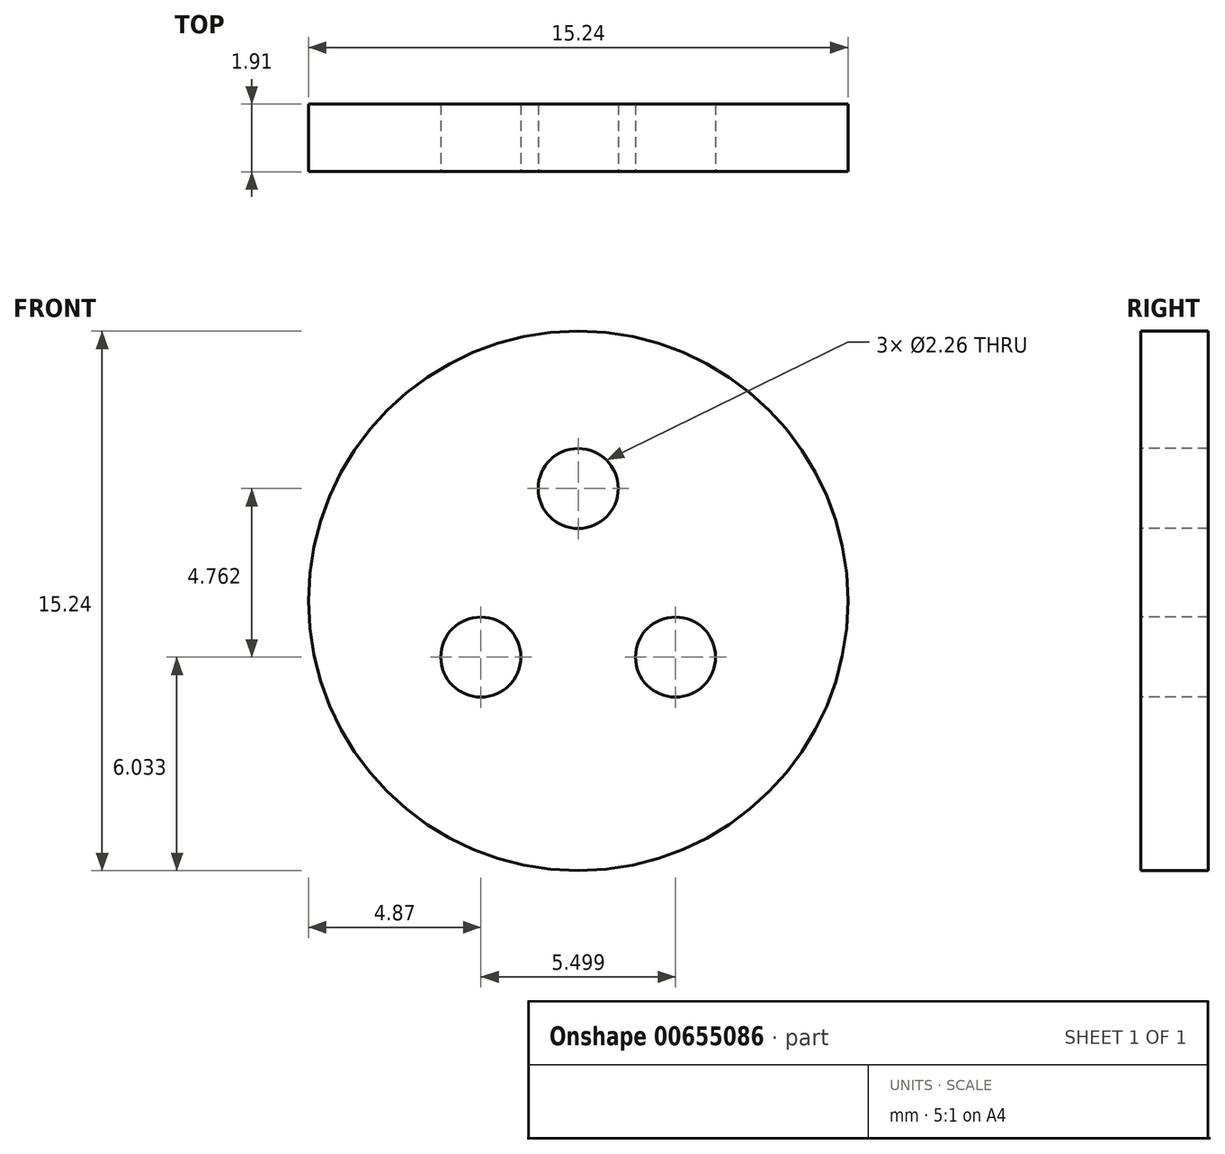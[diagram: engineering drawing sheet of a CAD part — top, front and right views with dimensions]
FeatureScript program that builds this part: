
annotation { "Feature Type Name" : "Feature", "Feature Type Description" : "" }
export const myFeature = defineFeature(function(context is Context, id is Id, definition is map)
    precondition{}
    {
        {
            var Q0;
            Q0=qCreatedBy(makeId("Front.planeOp"),FACE);
            var sketch = newSketch(context, id + "F0", { "sketchPlane" : qUnion([Q0])});
            skCircle(sketch, "E0", {"center": v(0, 0) * mm, "radius": 7.62 * mm});
            skSolve(sketch);
        }
        {
            var Q0;
            Q0 = qSketchRegion(id + "F0", true);
            extrude(context, id + "F1", {"entities" : qUnion([Q0]), "depth" : 1.9 * mm, "offsetDistance" : 25.4 * mm});
        }
        {
            var Q0;
            Q0=makeQuery(id+"F1.opExtrude","CAP_FACE",FACE,{"disambiguationData":[OSD([sQuery(id+"F0.wireOp",EDGE,"E0")])],"isStart":false});
            var sketch = newSketch(context, id + "F2", { "sketchPlane" : qUnion([Q0])});
            skPoint(sketch, "E1", {"position": v(0, 3.18) * mm});
            skPoint(sketch, "E2.1.0", {"position": v(-2.75, -1.59) * mm});
            skPoint(sketch, "E2.2.0", {"position": v(2.75, -1.59) * mm});
            skPoint(sketch, "E2.center", {"position": v(0, 0) * mm});
            skSolve(sketch);
        }
        {
            var Q0;
            Q0=sQuery(id+"F2.wireOp",VERTEX,"E1");
            var Q1;
            Q1=sQuery(id+"F2.wireOp",VERTEX,"E2.2.0");
            var Q2;
            Q2=sQuery(id+"F2.wireOp",VERTEX,"E2.1.0");
            var Q3;
            Q3=makeQuery(id+"F1.opExtrude","SWEPT_BODY",BODY,{"disambiguationData":[OSD([sQuery(id+"F0.wireOp",EDGE,"E0")])]});
            hole(context, id + "F3", {"style" : HoleStyle.SIMPLE, "endStyle" : HoleEndStyle.BLIND, "standardTappedOrClearance" : lookupTablePath({ "standard" : "ANSI", "engagement" : "75%", "pitch" : "40 tpi", "size" : "#4", "type" : "Tapped" }), "standardBlindInLast" : lookupTablePath({ "standard" : "ANSI", "engagement" : "75%", "pitch" : "40 tpi", "size" : "#4", "type" : "Tapped" }), "holeDiameter" : 2.26 * mm, "majorDiameter" : 2.84 * mm, "showTappedDepth" : true, "holeDepth" : 13.5 * mm, "isTappedThrough" : true, "tappedDepth" : 11.6 * mm, "tapClearance" : 3, "startFromSketch" : true, "locations" : qUnion([Q0, Q1, Q2]), "scope" : qUnion([Q3])});
        }
    });
